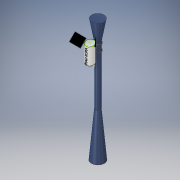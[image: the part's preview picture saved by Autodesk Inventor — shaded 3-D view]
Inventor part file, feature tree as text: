
AUTODESK INVENTOR PART (.ipt)
format: ipt  version: 2019 (Build 230136000, 136)  size: 655,360 bytes
history: native  units: mm
features: sketch x23, extrude x18, plane x11, fillet x6, chamfer x3, mirror x2, revolve x1, emboss x1
ambient origin geometry x8: Origin, YZ Plane, XZ Plane, XY Plane, X Axis, Y Axis, Z Axis, Center Point
bodies: Solid1 (feature_tree), Solid2 (feature_tree)
feature tree (65):
  extrude  "Extrusion1"  Depth=102.0mm
  plane  "Work Plane1"
  extrude  "Extrusion2"  Depth=55.75mm
  extrude  "Extrusion3"  Depth=2.0mm
  sketch  "Sketch4"  dims[d8=2.0mm d9=124.75mm d10=0.0mm]
  sketch  "Sketch5"  dims[d11=106.0mm d12=337.25mm d13=0.0mm]
  extrude  "Extrusion4"  Depth=124.75mm TaperAngle=0.0deg
  extrude  "Extrusion5"  Depth=337.25mm TaperAngle=0.0deg
  plane  "Work Plane2"
  extrude  "Extrusion6"  Depth=8.5mm TaperAngle=0.0deg
  extrude  "Extrusion7"  Depth=6.0mm TaperAngle=0.0deg
  plane  "Work Plane3"
  extrude  "Extrusion8"  Depth=4.25mm
  extrude  "Extrusion9"  Depth=38.5mm TaperAngle=0.0deg
  revolve  "Revolution1"  [1 undecoded]
  plane  "Work Plane4"
  extrude  "Extrusion10"  Depth=1.0mm
  fillet  "Fillet1"  Radius=1.0mm
  fillet  "Fillet2"  Radius=2.5mm
  fillet  "Fillet3"  Radius=2.25mm
  fillet  "Fillet4"  Radius=2.5mm
  fillet  "Fillet5"  [1 undecoded]
  sketch  "Sketch14"  dims[d55=3.0mm d56=0.0mm d57=2.0mm d58=2.0mm d59=45.0deg]
  plane  "Work Plane5"
  extrude  "Extrusion11"  Depth=4.75mm TaperAngle=45.0deg
  chamfer  "Chamfer1"  Distance=4.75mm Angle=45.0deg
  extrude  "Extrusion12"  Depth=2.0mm TaperAngle=45.0deg
  chamfer  "Chamfer2"  Distance=19.5mm
  extrude  "Extrusion13"  Depth=14.25mm TaperAngle=0.0deg
  chamfer  "Chamfer3"  Distance=1.0mm
  plane  "Work Plane6"
  extrude  "Extrusion14"  Depth=2.0mm TaperAngle=0.0deg
  plane  "Work Plane7"
  extrude  "Extrusion15"  Depth=270.0mm TaperAngle=0.0deg
  plane  "Work Plane8"
  mirror  "Mirror1"
  fillet  "Fillet6"  Radius=599.0mm
  plane  "Work Plane9"
  emboss  "Emboss2"
  plane  "Work Plane10"
  extrude  "Extrusion16"  [1 undecoded]
  plane  "Work Plane11"
  mirror  "Mirror2"
  extrude  "Extrusion17"  [1 undecoded]
  extrude  "Extrusion18"  [1 undecoded]
  sketch  "Sketch1"  dims[d0=106.0mm d1=102.0mm]
  sketch  "Sketch2"  dims[d2=250.0mm d3=0.0mm d4=55.75mm]
  sketch  "Sketch3"  dims[d5=109.5mm d6=0.0mm d7=2.0mm]
  sketch  "Sketch6"  dims[d14=20.0mm d15=8.5mm d16=5.75mm d17=0.0mm d18=0.0mm]
  sketch  "Sketch7"  dims[d19=-8.25mm d20=6.0mm d21=1.0mm d22=0.0mm d23=0.0mm]
  sketch  "Sketch8"  dims[d24=3.75mm d25=0.0mm d26=4.25mm]
  sketch  "Sketch9"  dims[d27=71.0mm d28=-0.349066mm d29=38.5mm d30=0.0mm]
  sketch  "Sketch10"  dims[d31=90.0deg d32=-105.25mm]
  sketch  "Sketch11"  dims[d33=7.75mm d34=0.0mm d35=1.0mm d36=1.0mm d37=2.5mm d38=2.25mm d39=2.5mm d40=-49.0mm]
  sketch  "Sketch12"  dims[d41=2.0mm d42=58.375mm d43=0.0mm d44=0.0mm d45=4.75mm d46=2.0mm d47=45.0deg]
  sketch  "Sketch13"  dims[d48=74.25mm d49=11.5mm d50=0.0mm d51=0.0mm d52=4.75mm d53=2.0mm d54=45.0deg]
  sketch  "Sketch15"  dims[d60=-49.75mm]
  sketch  "Sketch16"  dims[d61=14.0mm d62=19.5mm d63=0.0mm]
  sketch  "Sketch17"  dims[d64=-99.0mm d65=14.25mm d66=0.0mm]
  sketch  "Sketch18"  dims[d67=37.75mm]
  sketch  "Sketch19"  dims[d68=2.5mm]
  sketch  "Sketch21"  dims[d69=53.75mm d72=1.0mm d73=0.0mm]
  sketch  "Sketch22"  dims[d74=5.0mm d75=2.0mm d76=0.0mm]
  sketch  "Sketch23"  dims[d77=0.0mm d78=270.0mm d79=793.25mm d80=1.745329mm d81=0.0mm d82=599.0mm d83=0.872665mm]
  sketch  "Sketch24"
note: 5 required parameter values undecoded (feature->parameter linkage not recoverable at this tier; creation-order binding heuristic only, values carry confidence <= 0.55)